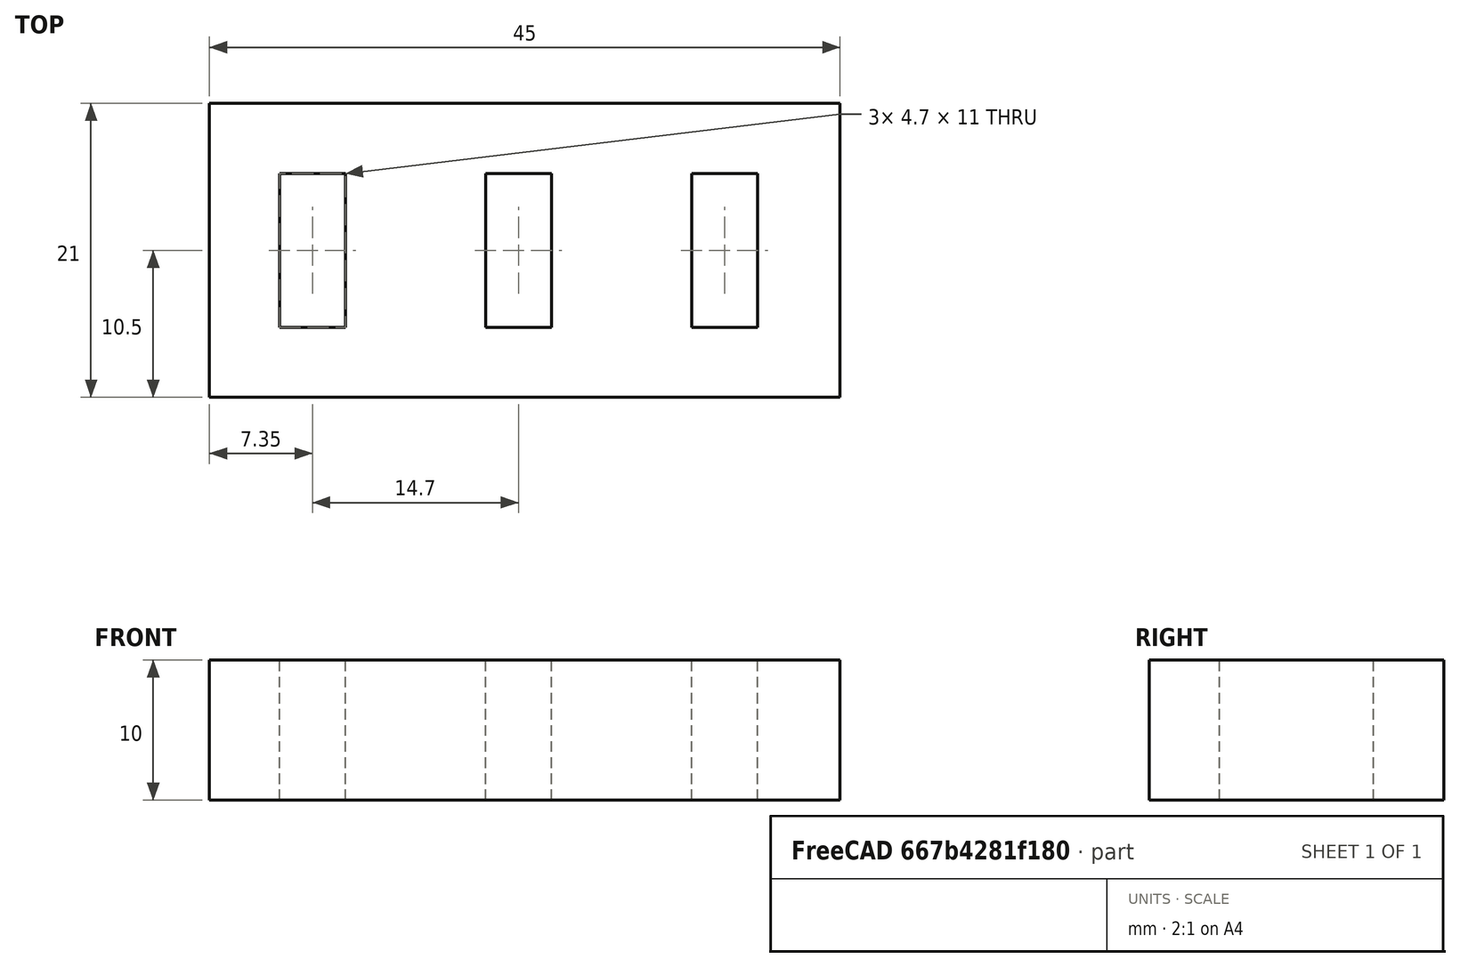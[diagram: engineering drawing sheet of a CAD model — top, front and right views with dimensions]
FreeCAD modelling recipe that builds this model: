
FCSTD DOCUMENT  (FreeCAD 1.0R39319 (Git))
Label: ojt1_t08p01_usb_flash
License: All rights reserved
LicenseURL: https://en.wikipedia.org/wiki/All_rights_reserved
objects: Part::Box×4, Part::Cut×3
note: 7 computed .brp shape members not serialized (recipe doc carries the construction recipe); baked Part::Feature solids carry a one-line shape summary decoded from their .brp

FEATURE [Part::Box] Box  label="Cub"
  AttacherType = Attacher::AttachEngine3D
  Height = 13
  Length = 4.7
  Placement = pos=(0,0,-1) rot=(0,0,1;0rad)
  Width = 11
FEATURE [Part::Box] Box001  label="Cub001"
  AttacherType = Attacher::AttachEngine3D
  Height = 13
  Length = 4.7
  Placement = pos=(14.7,0,-1) rot=(0,0,1;0rad)
  Width = 11
FEATURE [Part::Box] Box002  label="Cub002"
  AttacherType = Attacher::AttachEngine3D
  Height = 13
  Length = 4.7
  Placement = pos=(29.4,0,-1) rot=(0,0,1;0rad)
  Width = 11
FEATURE [Part::Box] Box003  label="Cub003"
  AttacherType = Attacher::AttachEngine3D
  Height = 10
  Length = 45
  Placement = pos=(-5,-5,0) rot=(0,0,1;0rad)
  Width = 21
FEATURE [Part::Cut] Cut
  Base = -> Box003
  Refine = true
  Tool = -> Box002
FEATURE [Part::Cut] Cut001
  Base = -> Cut
  Refine = true
  Tool = -> Box001
FEATURE [Part::Cut] Cut002
  Base = -> Cut001
  Refine = true
  Tool = -> Box
